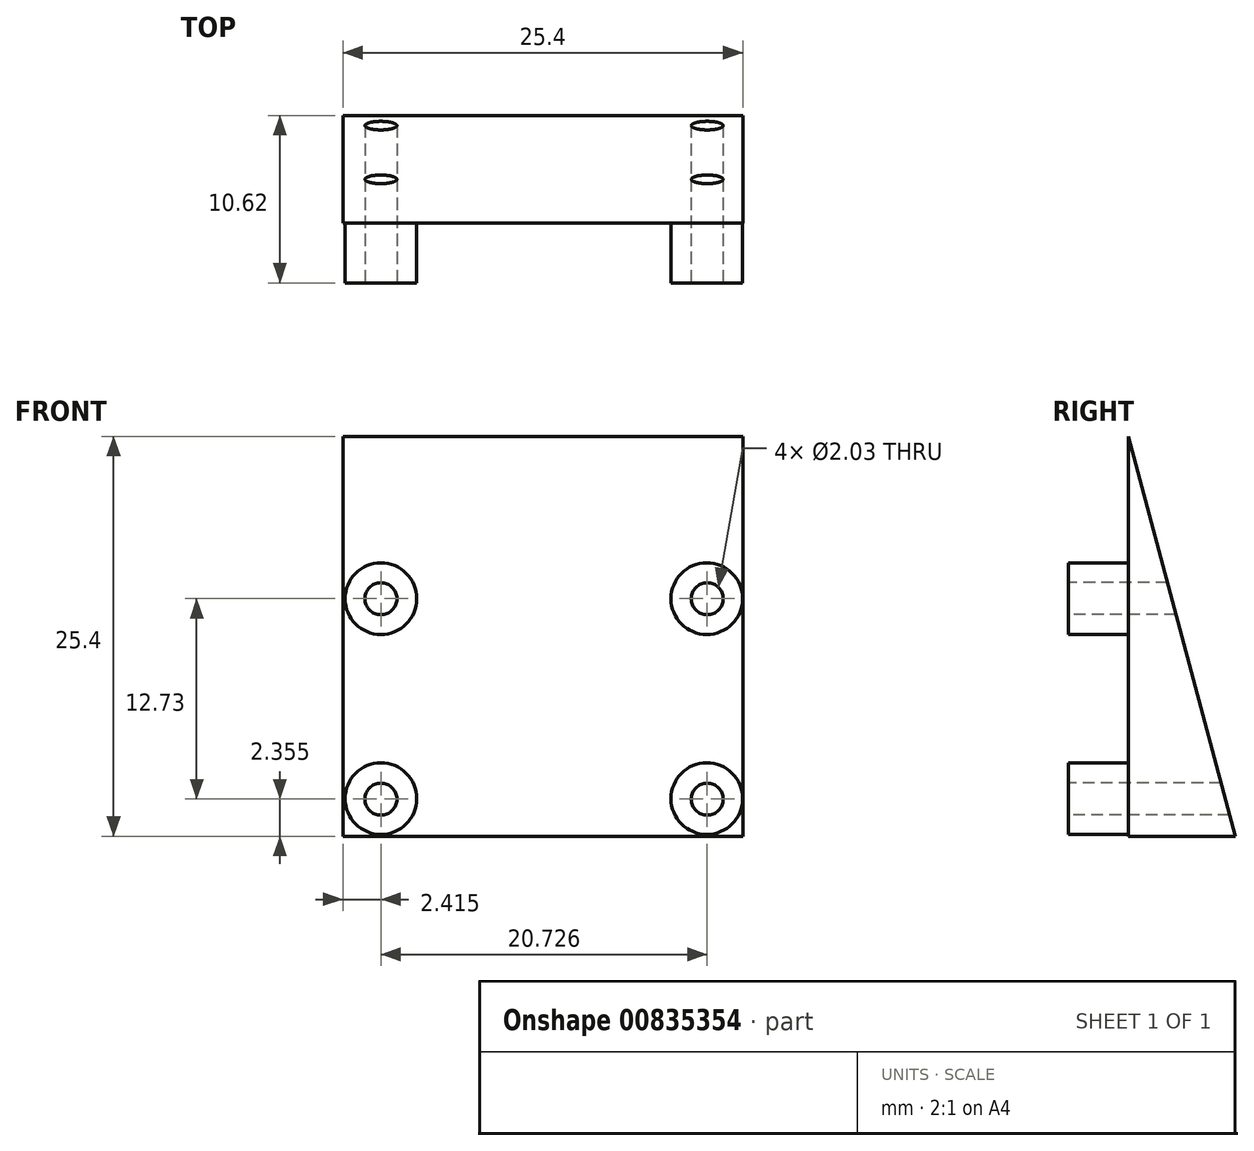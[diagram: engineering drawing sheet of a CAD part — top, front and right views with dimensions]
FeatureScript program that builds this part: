
annotation { "Feature Type Name" : "Feature", "Feature Type Description" : "" }
export const myFeature = defineFeature(function(context is Context, id is Id, definition is map)
    precondition{}
    {
        {
            var Q0;
            Q0=qCreatedBy(makeId("Right.planeOp"),FACE);
            var sketch = newSketch(context, id + "F0", { "sketchPlane" : qUnion([Q0])});
            skLineSegment(sketch, "E0", {"start": v(0, 12.7) * mm, "end": v(0, -12.7) * mm});
            skLineSegment(sketch, "E1", {"start": v(0, -12.7) * mm, "end": v(6.8, -12.7) * mm});
            skLineSegment(sketch, "E2", {"start": v(6.8, -12.7) * mm, "end": v(0, 12.7) * mm});
            skSolve(sketch);
        }
        {
            var Q0;
            Q0 = qSketchRegion(id + "F0", true);
            extrude(context, id + "F1", {"entities" : qUnion([Q0]), "endBound" : BoundingType.SYMMETRIC, "depth" : 25.4 * mm, "offsetDistance" : 25.4 * mm});
        }
        {
            var Q0;
            Q0=makeQuery(id+"F1.opExtrude","SWEPT_FACE",FACE,{"disambiguationData":[OSD([sQuery(id+"F0.wireOp",EDGE,"E0")])]});
            var sketch = newSketch(context, id + "F2", { "sketchPlane" : qUnion([Q0])});
            skCircle(sketch, "E3", {"center": v(-10.29, -10.32) * mm, "radius": 2.27 * mm});
            skCircle(sketch, "E4", {"center": v(10.41, -10.32) * mm, "radius": 2.27 * mm});
            skCircle(sketch, "E5", {"center": v(-10.29, 2.38) * mm, "radius": 2.27 * mm});
            skCircle(sketch, "E6", {"center": v(10.41, 2.38) * mm, "radius": 2.27 * mm});
            skSolve(sketch);
        }
        {
            var Q0;
            Q0 = qSketchRegion(id + "F2", true);
            extrude(context, id + "F3", {"entities" : qUnion([Q0]), "operationType" : NewBodyOperationType.ADD, "depth" : 3.8 * mm, "offsetDistance" : 25.4 * mm});
        }
        {
            var Q0;
            Q0=makeQuery(id+"F3.opExtrude","CAP_FACE",FACE,{"disambiguationData":[OSD([sQuery(id+"F2.wireOp",EDGE,"E5")])],"isStart":false});
            var sketch = newSketch(context, id + "F4", { "sketchPlane" : qUnion([Q0])});
            skCircle(sketch, "E7", {"center": v(-10.29, 2.38) * mm, "radius": 1.02 * mm});
            skCircle(sketch, "E8", {"center": v(-10.29, -10.35) * mm, "radius": 1.02 * mm});
            skCircle(sketch, "E9", {"center": v(10.44, 2.38) * mm, "radius": 1.02 * mm});
            skCircle(sketch, "E10", {"center": v(10.44, -10.35) * mm, "radius": 1.02 * mm});
            skSolve(sketch);
        }
        {
            var Q0;
            Q0 = qSketchRegion(id + "F4", true);
            extrude(context, id + "F5", {"entities" : qUnion([Q0]), "operationType" : NewBodyOperationType.REMOVE, "endBound" : BoundingType.THROUGH_ALL, "oppositeDirection" : true, "depth" : 25.4 * mm, "offsetDistance" : 25.4 * mm});
        }
    });
